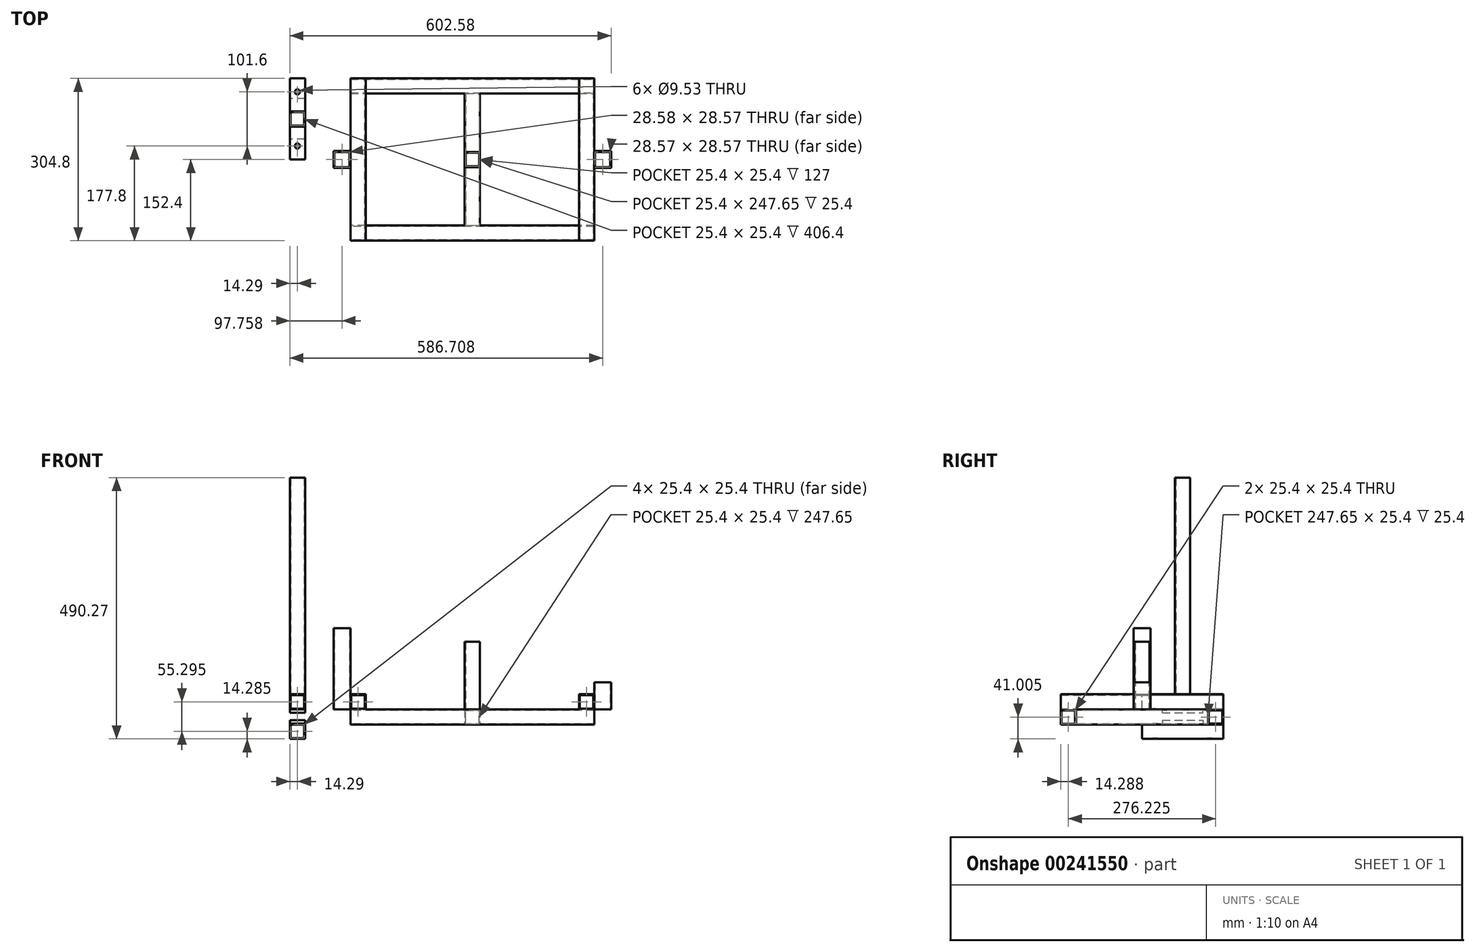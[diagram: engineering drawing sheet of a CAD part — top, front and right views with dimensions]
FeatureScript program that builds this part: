
annotation { "Feature Type Name" : "Feature", "Feature Type Description" : "" }
export const myFeature = defineFeature(function(context is Context, id is Id, definition is map)
    precondition{}
    {
        {
            var Q0;
            Q0=qCreatedBy(makeId("Front.planeOp"),FACE);
            var sketch = newSketch(context, id + "F0", { "sketchPlane" : qUnion([Q0])});
            skLineSegment(sketch, "E0.bottom", {"start": v(12.7, -12.7) * mm, "end": v(-12.7, -12.7) * mm});
            skLineSegment(sketch, "E0.top", {"start": v(12.7, 12.7) * mm, "end": v(-12.7, 12.7) * mm});
            skLineSegment(sketch, "E0.left", {"start": v(12.7, -12.7) * mm, "end": v(12.7, 12.7) * mm});
            skLineSegment(sketch, "E0.right", {"start": v(-12.7, -12.7) * mm, "end": v(-12.7, 12.7) * mm});
            skPoint(sketch, "E0.middle", {"position": v(0, 0) * mm});
            skLineSegment(sketch, "E1.bottom", {"start": v(14.29, -14.29) * mm, "end": v(-14.29, -14.29) * mm});
            skLineSegment(sketch, "E1.top", {"start": v(14.29, 14.29) * mm, "end": v(-14.29, 14.29) * mm});
            skLineSegment(sketch, "E1.left", {"start": v(14.29, -14.29) * mm, "end": v(14.29, 14.29) * mm});
            skLineSegment(sketch, "E1.right", {"start": v(-14.29, -14.29) * mm, "end": v(-14.29, 14.29) * mm});
            skSolve(sketch);
        }
        {
            var Q0;
            Q0=makeQuery(id+"F0.imprint","IMPRINT",FACE,{"disambiguationData":[TD([[makeQuery(id+"F0.imprint","IMPRINT",EDGE,{"derivedFrom":sQuery(id+"F0.wireOp",EDGE,"E0.bottom")}),1.0]])]});
            extrude(context, id + "F1", {"entities" : qUnion([Q0]), "depth" : 152.4 * mm});
        }
        {
            var Q0;
            Q0=makeQuery(id+"F1.opExtrude","SWEPT_FACE",FACE,{"disambiguationData":[OSD([sQuery(id+"F0.wireOp",EDGE,"E1.top")])]});
            var sketch = newSketch(context, id + "F2", { "sketchPlane" : qUnion([Q0])});
            skLineSegment(sketch, "E2.bottom", {"start": v(14.29, -90.49) * mm, "end": v(-14.29, -90.49) * mm});
            skLineSegment(sketch, "E2.top", {"start": v(14.29, -61.91) * mm, "end": v(-14.29, -61.91) * mm});
            skLineSegment(sketch, "E2.left", {"start": v(14.29, -90.49) * mm, "end": v(14.29, -61.91) * mm});
            skLineSegment(sketch, "E2.right", {"start": v(-14.29, -90.49) * mm, "end": v(-14.29, -61.91) * mm});
            skPoint(sketch, "E2.middle", {"position": v(0, -76.2) * mm});
            skLineSegment(sketch, "E3.bottom", {"start": v(12.7, -88.9) * mm, "end": v(-12.7, -88.9) * mm});
            skLineSegment(sketch, "E3.top", {"start": v(12.7, -63.5) * mm, "end": v(-12.7, -63.5) * mm});
            skLineSegment(sketch, "E3.left", {"start": v(12.7, -88.9) * mm, "end": v(12.7, -63.5) * mm});
            skLineSegment(sketch, "E3.right", {"start": v(-12.7, -88.9) * mm, "end": v(-12.7, -63.5) * mm});
            skPoint(sketch, "E4.start.orphan", {"position": v(-14.29, -76.2) * mm});
            skPoint(sketch, "E5.trimOffspring.end.orphan", {"position": v(14.29, -76.2) * mm});
            skSolve(sketch);
        }
        {
            var Q0;
            Q0=makeQuery(id+"F2.imprint","IMPRINT",FACE,{"disambiguationData":[TD([[makeQuery(id+"F2.imprint","IMPRINT",EDGE,{"derivedFrom":sQuery(id+"F2.wireOp",EDGE,"E2.bottom")}),-1.0]])]});
            extrude(context, id + "F3", {"entities" : qUnion([Q0]), "operationType" : NewBodyOperationType.ADD, "depth" : 406.4 * mm});
        }
        {
            var Q0;
            Q0=makeQuery(id+"F1.opExtrude","SWEPT_FACE",FACE,{"disambiguationData":[OSD([sQuery(id+"F0.wireOp",EDGE,"E1.bottom")])]});
            var sketch = newSketch(context, id + "F4", { "sketchPlane" : qUnion([Q0])});
            skLineSegment(sketch, "E6.bottom", {"start": v(14.29, 38.1) * mm, "end": v(-14.29, 38.1) * mm});
            skLineSegment(sketch, "E6.top", {"start": v(14.29, 114.3) * mm, "end": v(-14.29, 114.3) * mm});
            skLineSegment(sketch, "E6.left", {"start": v(14.29, 38.1) * mm, "end": v(14.29, 114.3) * mm});
            skLineSegment(sketch, "E6.right", {"start": v(-14.29, 38.1) * mm, "end": v(-14.29, 114.3) * mm});
            skPoint(sketch, "E6.middle", {"position": v(0, 76.2) * mm});
            skPoint(sketch, "E7.orphan", {"position": v(-14.29, 76.2) * mm});
            skPoint(sketch, "E8.end.orphan", {"position": v(14.29, 76.2) * mm});
            skSolve(sketch);
        }
        {
            var Q0;
            Q0=makeQuery(id+"F4.imprint","IMPRINT",FACE,{"disambiguationData":[TD([[makeQuery(id+"F4.imprint","IMPRINT",EDGE,{"derivedFrom":sQuery(id+"F4.wireOp",EDGE,"E6.bottom")}),-1.0]])]});
            extrude(context, id + "F5", {"entities" : qUnion([Q0]), "operationType" : NewBodyOperationType.ADD, "depth" : 6.35 * mm});
        }
        {
            var Q0;
            {var subQ2=sQuery(id+"F0.wireOp",EDGE,"E1.top");Q0=makeQuery(id+"F3.boolean.opBoolean","SPLIT",FACE,{"disambiguationData":[TD([makeQuery(id+"F3.opExtrude","SWEPT_FACE",FACE,{"disambiguationData":[OSD([sQuery(id+"F2.wireOp",EDGE,"E2.top")])]})])],"derivedFrom":makeQuery(id+"F1.opExtrude","SWEPT_FACE",FACE,{"disambiguationData":[OSD([subQ2])]})});}
            var sketch = newSketch(context, id + "F6", { "sketchPlane" : qUnion([Q0])});
            skLineSegment(sketch, "E9", {"start": v(0, 0) * mm, "end": v(0, -25.4) * mm});
            skPoint(sketch, "E9.endSnap0", {"position": v(0, 0) * mm});
            skLineSegment(sketch, "E10", {"start": v(0, -152.33) * mm, "end": v(0, -126.93) * mm});
            skSolve(sketch);
        }
        {
            var Q0;
            Q0=sQuery(id+"F6.wireOp",VERTEX,"E9.end");
            var Q1;
            Q1=sQuery(id+"F6.wireOp",VERTEX,"E10.end");
            var Q2;
            Q2=makeQuery(id+"F1.opExtrude","SWEPT_BODY",BODY,{"disambiguationData":[OSD([sQuery(id+"F0.wireOp",EDGE,"E0.bottom"),sQuery(id+"F0.wireOp",EDGE,"E0.top"),sQuery(id+"F0.wireOp",EDGE,"E0.left"),sQuery(id+"F0.wireOp",EDGE,"E0.right"),sQuery(id+"F0.wireOp",EDGE,"E1.bottom"),sQuery(id+"F0.wireOp",EDGE,"E1.top"),sQuery(id+"F0.wireOp",EDGE,"E1.left"),sQuery(id+"F0.wireOp",EDGE,"E1.right")])]});
            hole(context, id + "F7", {"style" : HoleStyle.SIMPLE, "endStyle" : HoleEndStyle.THROUGH, "holeDiameter" : 9.52 * mm, "startFromSketch" : true, "locations" : qUnion([Q0, Q1]), "scope" : qUnion([Q2]), "isTappedThrough" : true});
        }
        {
            var Q0;
            Q0=qCreatedBy(makeId("Front.planeOp"),FACE);
            var sketch = newSketch(context, id + "F8", { "sketchPlane" : qUnion([Q0])});
            skLineSegment(sketch, "E11.bottom", {"start": v(14.29, -69.58) * mm, "end": v(-14.29, -69.58) * mm});
            skLineSegment(sketch, "E11.top", {"start": v(14.29, -41) * mm, "end": v(-14.29, -41) * mm});
            skLineSegment(sketch, "E11.left", {"start": v(14.29, -69.58) * mm, "end": v(14.29, -41) * mm});
            skLineSegment(sketch, "E11.right", {"start": v(-14.29, -69.58) * mm, "end": v(-14.29, -41) * mm});
            skPoint(sketch, "E11.middle", {"position": v(0, -55.3) * mm});
            skLineSegment(sketch, "E12.bottom", {"start": v(12.7, -68) * mm, "end": v(-12.7, -68) * mm});
            skLineSegment(sketch, "E12.top", {"start": v(12.7, -42.6) * mm, "end": v(-12.7, -42.6) * mm});
            skLineSegment(sketch, "E12.left", {"start": v(12.7, -68) * mm, "end": v(12.7, -42.6) * mm});
            skLineSegment(sketch, "E12.right", {"start": v(-12.7, -68) * mm, "end": v(-12.7, -42.6) * mm});
            skSolve(sketch);
        }
        {
            var Q0;
            Q0=makeQuery(id+"F8.imprint","IMPRINT",FACE,{"disambiguationData":[TD([[makeQuery(id+"F8.imprint","IMPRINT",EDGE,{"derivedFrom":sQuery(id+"F8.wireOp",EDGE,"E11.bottom")}),-1.0]])]});
            extrude(context, id + "F9", {"entities" : qUnion([Q0]), "depth" : 152.4 * mm});
        }
        {
            var Q0;
            Q0=makeQuery(id+"F9.opExtrude","SWEPT_FACE",FACE,{"disambiguationData":[OSD([sQuery(id+"F8.wireOp",EDGE,"E11.top")])]});
            var sketch = newSketch(context, id + "F10", { "sketchPlane" : qUnion([Q0])});
            skLineSegment(sketch, "E13.bottom", {"start": v(14.29, -38.1) * mm, "end": v(-14.29, -38.1) * mm});
            skLineSegment(sketch, "E13.top", {"start": v(14.29, -114.3) * mm, "end": v(-14.29, -114.3) * mm});
            skLineSegment(sketch, "E13.left", {"start": v(14.29, -38.1) * mm, "end": v(14.29, -114.3) * mm});
            skLineSegment(sketch, "E13.right", {"start": v(-14.29, -38.1) * mm, "end": v(-14.29, -114.3) * mm});
            skPoint(sketch, "E13.middle", {"position": v(0, -76.2) * mm});
            skPoint(sketch, "E14.orphan", {"position": v(14.29, -76.2) * mm});
            skPoint(sketch, "E15.start.orphan", {"position": v(-14.29, -76.2) * mm});
            skSolve(sketch);
        }
        {
            var Q0;
            Q0=makeQuery(id+"F10.imprint","IMPRINT",FACE,{"disambiguationData":[TD([[makeQuery(id+"F10.imprint","IMPRINT",EDGE,{"derivedFrom":sQuery(id+"F10.wireOp",EDGE,"E13.bottom")}),1.0]])]});
            extrude(context, id + "F11", {"entities" : qUnion([Q0]), "operationType" : NewBodyOperationType.ADD, "depth" : 6.35 * mm});
        }
        {
            var Q0;
            Q0=makeQuery(id+"F9.opExtrude","SWEPT_FACE",FACE,{"disambiguationData":[OSD([sQuery(id+"F8.wireOp",EDGE,"E11.bottom")])]});
            var sketch = newSketch(context, id + "F12", { "sketchPlane" : qUnion([Q0])});
            skLineSegment(sketch, "E16", {"start": v(0, 152.4) * mm, "end": v(0, 127) * mm});
            skPoint(sketch, "E16.endSnap0", {"position": v(0, 152.4) * mm});
            skLineSegment(sketch, "E17", {"start": v(0, 0) * mm, "end": v(0, 25.4) * mm});
            skSolve(sketch);
        }
        {
            var Q0;
            Q0=sQuery(id+"F12.wireOp",VERTEX,"E16.end");
            var Q1;
            Q1=sQuery(id+"F12.wireOp",VERTEX,"E17.end");
            var Q2;
            Q2=makeQuery(id+"F1.opExtrude","SWEPT_BODY",BODY,{"disambiguationData":[OSD([sQuery(id+"F0.wireOp",EDGE,"E0.bottom"),sQuery(id+"F0.wireOp",EDGE,"E0.top"),sQuery(id+"F0.wireOp",EDGE,"E0.left"),sQuery(id+"F0.wireOp",EDGE,"E0.right"),sQuery(id+"F0.wireOp",EDGE,"E1.bottom"),sQuery(id+"F0.wireOp",EDGE,"E1.top"),sQuery(id+"F0.wireOp",EDGE,"E1.left"),sQuery(id+"F0.wireOp",EDGE,"E1.right")])]});
            var Q3;
            Q3=makeQuery(id+"F9.opExtrude","SWEPT_BODY",BODY,{"disambiguationData":[OSD([sQuery(id+"F8.wireOp",EDGE,"E11.bottom"),sQuery(id+"F8.wireOp",EDGE,"E11.top"),sQuery(id+"F8.wireOp",EDGE,"E11.left"),sQuery(id+"F8.wireOp",EDGE,"E11.right"),sQuery(id+"F8.wireOp",EDGE,"E12.bottom"),sQuery(id+"F8.wireOp",EDGE,"E12.top"),sQuery(id+"F8.wireOp",EDGE,"E12.left"),sQuery(id+"F8.wireOp",EDGE,"E12.right")])]});
            hole(context, id + "F13", {"style" : HoleStyle.SIMPLE, "endStyle" : HoleEndStyle.THROUGH, "holeDiameter" : 9.52 * mm, "startFromSketch" : true, "locations" : qUnion([Q0, Q1]), "scope" : qUnion([Q2, Q3]), "isTappedThrough" : true});
        }
        {
            var Q0;
            Q0=qCreatedBy(makeId("Front.planeOp"),FACE);
            var sketch = newSketch(context, id + "F14", { "sketchPlane" : qUnion([Q0])});
            skLineSegment(sketch, "E18.bottom", {"start": v(127.92, -14.29) * mm, "end": v(99.34, -14.29) * mm});
            skLineSegment(sketch, "E18.top", {"start": v(127.92, 14.29) * mm, "end": v(99.34, 14.29) * mm});
            skLineSegment(sketch, "E18.left", {"start": v(127.92, -14.29) * mm, "end": v(127.92, 14.29) * mm});
            skLineSegment(sketch, "E18.right", {"start": v(99.34, -14.29) * mm, "end": v(99.34, 14.29) * mm});
            skPoint(sketch, "E18.middle", {"position": v(113.63, 0) * mm});
            skLineSegment(sketch, "E19.bottom", {"start": v(126.33, -12.7) * mm, "end": v(100.93, -12.7) * mm});
            skLineSegment(sketch, "E19.top", {"start": v(126.33, 12.7) * mm, "end": v(100.93, 12.7) * mm});
            skLineSegment(sketch, "E19.left", {"start": v(126.33, -12.7) * mm, "end": v(126.33, 12.7) * mm});
            skLineSegment(sketch, "E19.right", {"start": v(100.93, -12.7) * mm, "end": v(100.93, 12.7) * mm});
            skSolve(sketch);
        }
        {
            var Q0;
            Q0=makeQuery(id+"F14.imprint","IMPRINT",FACE,{"disambiguationData":[TD([[makeQuery(id+"F14.imprint","IMPRINT",EDGE,{"derivedFrom":sQuery(id+"F14.wireOp",EDGE,"E18.bottom")}),-1.0]])]});
            extrude(context, id + "F15", {"entities" : qUnion([Q0]), "depth" : 304.8 * mm});
        }
        {
            var Q0;
            Q0=makeQuery(id+"F15.opExtrude","SWEPT_FACE",FACE,{"disambiguationData":[OSD([sQuery(id+"F14.wireOp",EDGE,"E18.right")])]});
            var sketch = newSketch(context, id + "F16", { "sketchPlane" : qUnion([Q0])});
            skLineSegment(sketch, "E20", {"start": v(304.8, -14.29) * mm, "end": v(304.8, -42.86) * mm});
            skLineSegment(sketch, "E21", {"start": v(304.8, -42.86) * mm, "end": v(276.23, -42.86) * mm});
            skLineSegment(sketch, "E22", {"start": v(276.23, -42.86) * mm, "end": v(276.23, -14.29) * mm});
            skLineSegment(sketch, "E23.bottom", {"start": v(303.21, -41.28) * mm, "end": v(277.81, -41.28) * mm});
            skLineSegment(sketch, "E23.top", {"start": v(303.21, -15.88) * mm, "end": v(277.81, -15.88) * mm});
            skLineSegment(sketch, "E23.left", {"start": v(303.21, -41.28) * mm, "end": v(303.21, -15.88) * mm});
            skLineSegment(sketch, "E23.right", {"start": v(277.81, -41.28) * mm, "end": v(277.81, -15.88) * mm});
            skPoint(sketch, "E23.middle", {"position": v(290.51, -28.58) * mm});
            skPoint(sketch, "E24.trimOffspring.end.orphan", {"position": v(304.8, -28.58) * mm});
            skPoint(sketch, "E25.trimOffspring.end.orphan", {"position": v(290.51, -14.29) * mm});
            skPoint(sketch, "E26.start.orphan", {"position": v(276.23, -28.58) * mm});
            skPoint(sketch, "E27.start.orphan", {"position": v(290.51, -42.86) * mm});
            skSolve(sketch);
        }
        {
            var Q0;
            {var subQ1=sQuery(id+"F16.wireOp",EDGE,"E20");Q0=makeQuery(id+"F16.imprint","IMPRINT",FACE,{"disambiguationData":[TD([[makeQuery(id+"F16.imprint","IMPRINT",EDGE,{"derivedFrom":subQ1}),-1.0]])]});}
            extrude(context, id + "F17", {"entities" : qUnion([Q0]), "operationType" : NewBodyOperationType.ADD, "oppositeDirection" : true, "depth" : 457.2 * mm});
        }
        {
            var Q0;
            Q0=makeQuery(id+"F17.boolean.opBoolean","MERGE",FACE,{"derivedFrom":[makeQuery(id+"F15.opExtrude","CAP_FACE",FACE,{"disambiguationData":[OSD([sQuery(id+"F14.wireOp",EDGE,"E18.bottom"),sQuery(id+"F14.wireOp",EDGE,"E18.top"),sQuery(id+"F14.wireOp",EDGE,"E18.left"),sQuery(id+"F14.wireOp",EDGE,"E18.right"),sQuery(id+"F14.wireOp",EDGE,"E19.bottom"),sQuery(id+"F14.wireOp",EDGE,"E19.top"),sQuery(id+"F14.wireOp",EDGE,"E19.left"),sQuery(id+"F14.wireOp",EDGE,"E19.right")])],"isStart":false}),makeQuery(id+"F17.opExtrude","SWEPT_FACE",FACE,{"disambiguationData":[OSD([sQuery(id+"F16.wireOp",EDGE,"E20")])]})]});
            var sketch = newSketch(context, id + "F18", { "sketchPlane" : qUnion([Q0])});
            skLineSegment(sketch, "E28", {"start": v(556.54, -14.29) * mm, "end": v(556.54, 14.29) * mm});
            skLineSegment(sketch, "E29", {"start": v(556.54, 14.29) * mm, "end": v(527.97, 14.29) * mm});
            skLineSegment(sketch, "E30", {"start": v(527.97, 14.29) * mm, "end": v(527.97, -14.29) * mm});
            skPoint(sketch, "E31.endSnap0", {"position": v(542.26, 0) * mm});
            skLineSegment(sketch, "E32.bottom", {"start": v(554.96, -12.7) * mm, "end": v(529.56, -12.7) * mm});
            skLineSegment(sketch, "E32.top", {"start": v(554.96, 12.7) * mm, "end": v(529.56, 12.7) * mm});
            skLineSegment(sketch, "E32.left", {"start": v(554.96, -12.7) * mm, "end": v(554.96, 12.7) * mm});
            skLineSegment(sketch, "E32.right", {"start": v(529.56, -12.7) * mm, "end": v(529.56, 12.7) * mm});
            skPoint(sketch, "E33.trimOffspring.end.orphan", {"position": v(556.54, 0) * mm});
            skPoint(sketch, "E31.start.orphan", {"position": v(542.26, 14.29) * mm});
            skPoint(sketch, "E34.start.orphan", {"position": v(527.97, 0) * mm});
            skPoint(sketch, "E35.trimOffspring.end.orphan", {"position": v(542.26, -14.29) * mm});
            skSolve(sketch);
        }
        {
            var Q0;
            {var subQ1=sQuery(id+"F18.wireOp",EDGE,"E28");Q0=makeQuery(id+"F18.imprint","IMPRINT",FACE,{"disambiguationData":[TD([[makeQuery(id+"F18.imprint","IMPRINT",EDGE,{"derivedFrom":subQ1}),1.0]])]});}
            extrude(context, id + "F19", {"entities" : qUnion([Q0]), "operationType" : NewBodyOperationType.ADD, "oppositeDirection" : true, "depth" : 304.8 * mm});
        }
        {
            var Q0;
            Q0=makeQuery(id+"F17.opExtrude","SWEPT_FACE",FACE,{"disambiguationData":[OSD([sQuery(id+"F16.wireOp",EDGE,"E22")])]});
            var sketch = newSketch(context, id + "F20", { "sketchPlane" : qUnion([Q0])});
            skLineSegment(sketch, "E36.bottom", {"start": v(-313.66, -14.29) * mm, "end": v(-342.23, -14.29) * mm});
            skLineSegment(sketch, "E36.top", {"start": v(-313.66, -42.86) * mm, "end": v(-342.23, -42.86) * mm});
            skLineSegment(sketch, "E36.left", {"start": v(-313.66, -14.29) * mm, "end": v(-313.66, -42.86) * mm});
            skLineSegment(sketch, "E36.right", {"start": v(-342.23, -14.29) * mm, "end": v(-342.23, -42.86) * mm});
            skPoint(sketch, "E36.middle", {"position": v(-327.94, -28.58) * mm});
            skLineSegment(sketch, "E37.bottom", {"start": v(-315.24, -41.28) * mm, "end": v(-340.64, -41.28) * mm});
            skLineSegment(sketch, "E37.top", {"start": v(-315.24, -15.88) * mm, "end": v(-340.64, -15.88) * mm});
            skLineSegment(sketch, "E37.left", {"start": v(-315.24, -41.28) * mm, "end": v(-315.24, -15.88) * mm});
            skLineSegment(sketch, "E37.right", {"start": v(-340.64, -41.28) * mm, "end": v(-340.64, -15.88) * mm});
            skPoint(sketch, "E38.trimOffspring.end.orphan", {"position": v(-327.94, -14.29) * mm});
            skPoint(sketch, "E39.start.orphan", {"position": v(-327.94, -42.86) * mm});
            skSolve(sketch);
        }
        {
            var Q0;
            Q0=makeQuery(id+"F20.imprint","IMPRINT",FACE,{"disambiguationData":[TD([[makeQuery(id+"F20.imprint","IMPRINT",EDGE,{"derivedFrom":sQuery(id+"F20.wireOp",EDGE,"E36.bottom")}),-1.0]])]});
            extrude(context, id + "F21", {"entities" : qUnion([Q0]), "operationType" : NewBodyOperationType.ADD, "depth" : 247.65 * mm});
        }
        {
            var Q0;
            Q0=makeQuery(id+"F19.boolean.opBoolean","MERGE",FACE,{"derivedFrom":[makeQuery(id+"F17.opExtrude","CAP_FACE",FACE,{"disambiguationData":[OSD([sQuery(id+"F14.wireOp",EDGE,"E18.bottom"),sQuery(id+"F14.wireOp",EDGE,"E18.right"),sQuery(id+"F16.wireOp",EDGE,"E20"),sQuery(id+"F16.wireOp",EDGE,"E21"),sQuery(id+"F16.wireOp",EDGE,"E22"),sQuery(id+"F16.wireOp",EDGE,"E23.bottom"),sQuery(id+"F16.wireOp",EDGE,"E23.top"),sQuery(id+"F16.wireOp",EDGE,"E23.left"),sQuery(id+"F16.wireOp",EDGE,"E23.right")])],"isStart":false}),makeQuery(id+"F19.opExtrude","SWEPT_FACE",FACE,{"disambiguationData":[OSD([sQuery(id+"F18.wireOp",EDGE,"E28")])]})]});
            var sketch = newSketch(context, id + "F22", { "sketchPlane" : qUnion([Q0])});
            skLineSegment(sketch, "E40", {"start": v(0, -14.29) * mm, "end": v(0, -42.86) * mm});
            skLineSegment(sketch, "E41", {"start": v(0, -42.86) * mm, "end": v(-28.57, -42.86) * mm});
            skLineSegment(sketch, "E42", {"start": v(-28.57, -42.86) * mm, "end": v(-28.57, -14.29) * mm});
            skLineSegment(sketch, "E43.bottom", {"start": v(-1.59, -15.88) * mm, "end": v(-26.99, -15.88) * mm});
            skLineSegment(sketch, "E43.top", {"start": v(-1.59, -41.28) * mm, "end": v(-26.99, -41.28) * mm});
            skLineSegment(sketch, "E43.left", {"start": v(-1.59, -15.88) * mm, "end": v(-1.59, -41.28) * mm});
            skLineSegment(sketch, "E43.right", {"start": v(-26.99, -15.88) * mm, "end": v(-26.99, -41.28) * mm});
            skPoint(sketch, "E43.middle", {"position": v(-14.29, -28.58) * mm});
            skPoint(sketch, "E44.trimOffspring.end.orphan", {"position": v(-14.29, -14.29) * mm});
            skPoint(sketch, "E45.start.orphan", {"position": v(-14.29, -42.86) * mm});
            skSolve(sketch);
        }
        {
            var Q0;
            {var subQ1=sQuery(id+"F22.wireOp",EDGE,"E40");Q0=makeQuery(id+"F22.imprint","IMPRINT",FACE,{"disambiguationData":[TD([[makeQuery(id+"F22.imprint","IMPRINT",EDGE,{"derivedFrom":subQ1}),-1.0]])]});}
            extrude(context, id + "F23", {"entities" : qUnion([Q0]), "operationType" : NewBodyOperationType.ADD, "oppositeDirection" : true, "depth" : 457.2 * mm});
        }
        {
            var Q0;
            {var subQ0=sQuery(id+"F14.wireOp",EDGE,"E18.right");var subQ1=sQuery(id+"F14.wireOp",EDGE,"E18.bottom");Q0=makeQuery(id+"F23.boolean.opBoolean","MERGE",FACE,{"derivedFrom":[makeQuery(id+"F21.boolean.opBoolean","MERGE",FACE,{"derivedFrom":[makeQuery(id+"F17.opExtrude","SWEPT_FACE",FACE,{"disambiguationData":[OSD([subQ1,subQ0])]}),makeQuery(id+"F21.opExtrude","SWEPT_FACE",FACE,{"disambiguationData":[OSD([sQuery(id+"F20.wireOp",EDGE,"E36.bottom")])]})]}),makeQuery(id+"F23.opExtrude","SWEPT_FACE",FACE,{"disambiguationData":[OSD([subQ1,subQ0,sQuery(id+"F16.wireOp",EDGE,"E20"),sQuery(id+"F18.wireOp",EDGE,"E28")])]})]});}
            var sketch = newSketch(context, id + "F24", { "sketchPlane" : qUnion([Q0])});
            skLineSegment(sketch, "E46.bottom", {"start": v(342.23, -138.11) * mm, "end": v(313.66, -138.11) * mm});
            skLineSegment(sketch, "E46.top", {"start": v(342.23, -166.69) * mm, "end": v(313.66, -166.69) * mm});
            skLineSegment(sketch, "E46.left", {"start": v(342.23, -138.11) * mm, "end": v(342.23, -166.69) * mm});
            skLineSegment(sketch, "E46.right", {"start": v(313.66, -138.11) * mm, "end": v(313.66, -166.69) * mm});
            skPoint(sketch, "E46.middle", {"position": v(327.94, -152.4) * mm});
            skLineSegment(sketch, "E47.bottom", {"start": v(340.64, -139.7) * mm, "end": v(315.24, -139.7) * mm});
            skLineSegment(sketch, "E47.top", {"start": v(340.64, -165.1) * mm, "end": v(315.24, -165.1) * mm});
            skLineSegment(sketch, "E47.left", {"start": v(340.64, -139.7) * mm, "end": v(340.64, -165.1) * mm});
            skLineSegment(sketch, "E47.right", {"start": v(315.24, -139.7) * mm, "end": v(315.24, -165.1) * mm});
            skPoint(sketch, "E48.start.orphan", {"position": v(313.66, -152.4) * mm});
            skPoint(sketch, "E49.trimOffspring.end.orphan", {"position": v(342.23, -152.4) * mm});
            skSolve(sketch);
        }
        {
            var Q0;
            Q0=makeQuery(id+"F24.imprint","IMPRINT",FACE,{"disambiguationData":[TD([[makeQuery(id+"F24.imprint","IMPRINT",EDGE,{"derivedFrom":sQuery(id+"F24.wireOp",EDGE,"E46.bottom")}),1.0]])]});
            extrude(context, id + "F25", {"entities" : qUnion([Q0]), "operationType" : NewBodyOperationType.ADD, "depth" : 127 * mm});
        }
        {
            var Q0;
            Q0=makeQuery(id+"F15.opExtrude","SWEPT_FACE",FACE,{"disambiguationData":[OSD([sQuery(id+"F14.wireOp",EDGE,"E18.bottom")])]});
            var sketch = newSketch(context, id + "F26", { "sketchPlane" : qUnion([Q0])});
            skLineSegment(sketch, "E50", {"start": v(99.34, 152.4) * mm, "end": v(97.76, 152.4) * mm});
            skLineSegment(sketch, "E51.bottom", {"start": v(97.76, 166.69) * mm, "end": v(69.18, 166.69) * mm});
            skLineSegment(sketch, "E51.top", {"start": v(97.76, 138.11) * mm, "end": v(69.18, 138.11) * mm});
            skLineSegment(sketch, "E51.left", {"start": v(97.76, 166.69) * mm, "end": v(97.76, 138.11) * mm});
            skLineSegment(sketch, "E51.right", {"start": v(69.18, 166.69) * mm, "end": v(69.18, 138.11) * mm});
            skPoint(sketch, "E51.middle", {"position": v(83.47, 152.4) * mm});
            skLineSegment(sketch, "E52.bottom", {"start": v(99.34, 168.28) * mm, "end": v(67.6, 168.28) * mm});
            skLineSegment(sketch, "E52.top", {"start": v(99.34, 136.53) * mm, "end": v(67.6, 136.53) * mm});
            skLineSegment(sketch, "E52.left", {"start": v(99.34, 168.28) * mm, "end": v(99.34, 136.53) * mm});
            skLineSegment(sketch, "E52.right", {"start": v(67.6, 168.28) * mm, "end": v(67.6, 136.53) * mm});
            skSolve(sketch);
        }
        {
            var Q0;
            {var subQ4=sQuery(id+"F26.wireOp",EDGE,"E51.bottom");Q0=makeQuery(id+"F26.imprint","IMPRINT",FACE,{"disambiguationData":[TD([[makeQuery(id+"F26.imprint","IMPRINT",EDGE,{"derivedFrom":subQ4}),-1.0]])]});}
            extrude(context, id + "F27", {"entities" : qUnion([Q0]), "operationType" : NewBodyOperationType.ADD, "oppositeDirection" : true, "depth" : 152.4 * mm});
        }
        {
            var Q0;
            Q0=makeQuery(id+"F19.opExtrude","SWEPT_FACE",FACE,{"disambiguationData":[OSD([sQuery(id+"F14.wireOp",EDGE,"E18.bottom"),sQuery(id+"F14.wireOp",EDGE,"E18.right"),sQuery(id+"F16.wireOp",EDGE,"E20")])]});
            var sketch = newSketch(context, id + "F28", { "sketchPlane" : qUnion([Q0])});
            skLineSegment(sketch, "E53", {"start": v(556.54, 152.4) * mm, "end": v(558.13, 152.4) * mm});
            skPoint(sketch, "E53.endSnap0", {"position": v(556.54, 152.4) * mm});
            skLineSegment(sketch, "E54.bottom", {"start": v(588.3, 136.52) * mm, "end": v(556.54, 136.52) * mm});
            skLineSegment(sketch, "E54.top", {"start": v(588.3, 168.27) * mm, "end": v(556.54, 168.27) * mm});
            skLineSegment(sketch, "E54.left", {"start": v(588.3, 136.52) * mm, "end": v(588.3, 168.27) * mm});
            skLineSegment(sketch, "E54.right", {"start": v(556.54, 136.52) * mm, "end": v(556.54, 168.27) * mm});
            skPoint(sketch, "E54.middle", {"position": v(572.42, 152.4) * mm});
            skLineSegment(sketch, "E55.bottom", {"start": v(586.7, 138.11) * mm, "end": v(558.13, 138.11) * mm});
            skLineSegment(sketch, "E55.top", {"start": v(586.7, 166.69) * mm, "end": v(558.13, 166.69) * mm});
            skLineSegment(sketch, "E55.left", {"start": v(586.7, 138.11) * mm, "end": v(586.7, 166.69) * mm});
            skLineSegment(sketch, "E55.right", {"start": v(558.13, 138.11) * mm, "end": v(558.13, 166.69) * mm});
            skSolve(sketch);
        }
        {
            var Q0;
            {var subQ2=sQuery(id+"F28.wireOp",EDGE,"E54.bottom");Q0=makeQuery(id+"F28.imprint","IMPRINT",FACE,{"disambiguationData":[TD([[makeQuery(id+"F28.imprint","IMPRINT",EDGE,{"derivedFrom":subQ2}),-1.0]])]});}
            extrude(context, id + "F29", {"entities" : qUnion([Q0]), "operationType" : NewBodyOperationType.ADD, "oppositeDirection" : true, "depth" : 50.8 * mm});
        }
    });
